# Revit family: KR6070001_Jabonera Dispensador Koral
name_source: partatom
category: Furniture
units: mm (PartAtom-declared; Revit-internal decimal feet)

## family parameters
Always vertical = Yes
Cut with Voids When Loaded = No
Host = Wall
OmniClass Number = 23.21.43.15.21
OmniClass Title = Institutional Soap Dispensers
Room Calculation Point = No
Shared = No

## types (1)
- Type 1
    Colección = Koral
    Creado por = BIMBAU
    Default Elevation = 0 mm  [stored 0 ft]
    Description = Instala en tu baño el dispensador de jabón Koral, que se convertirá en el complemento ideal para tu grifería y es combinable con las demás piezas de accesorios Koral. Con resistencia a la carga hasta de 9kg. ¡Adquiérelo ahora!
    Fecha de creación = 08/04/2021
    Garantía = 30 años en estructura
    Garantía Acabados = 3 años en acabado
    Manufacturer = Corona
    Material = Corona_Cromado
    Referencia = KR6070001
    Resistencia = Resistente a la corrosión, pelado y decoloración por agua.
    Temperatura de uso = De 4º C a 40º C (40º F y 104º F)
    URL = https://corona.co

note: [stored X ft] marks values corroborated as IEEE doubles in the binary element streams (Revit-internal decimal feet)

## geometry (parser evidence)
native form markers: Sweep x7
no freeform markers — native parametric forms only
